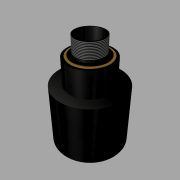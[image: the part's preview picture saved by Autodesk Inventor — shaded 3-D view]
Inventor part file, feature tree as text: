
AUTODESK INVENTOR PART (.ipt)
format: ipt  version: 2019 (Build 230136000, 136)  size: 198,144 bytes
history: native  units: mm
features: sketch x11, extrude x8, other x3, revolve x2, thread x1
ambient origin geometry x8: Origin, YZ Plane, XZ Plane, XY Plane, X Axis, Y Axis, Z Axis, Center Point
bodies: Solid1 (feature_tree), Solid2 (feature_tree), Solid3 (feature_tree), Solid4 (feature_tree)
feature tree (25):
  extrude  "Extrusion1"  Depth=7.0mm
  thread  "Thread1"  [1 undecoded]
  extrude  "Extrusion2"  Depth=15.0mm
  extrude  "Extrusion3"  Depth=0.25mm
  extrude  "Extrusion4"  Depth=0.25mm TaperAngle=0.0deg
  extrude  "Extrusion5"  Depth=19.0mm
  extrude  "Extrusion6"  Depth=10.5mm
  extrude  "Extrusion7"  Depth=4.0mm TaperAngle=0.0deg
  other  "Large Optic"
  extrude  "Extrusion8"  Depth=20.0mm TaperAngle=0.0deg
  other  "Large Optic Lens"
  sketch  "Sketch9"  dims[d25=-5.0mm d26=0.15mm]
  revolve  "Revolution1"  [1 undecoded]
  other  "Small Optic Lens"
  revolve  "Revolution2"  [1 undecoded]
  sketch  "Sketch1"  dims[d0=11.85mm d1=0.6mm d2=7.0mm d3=0.0mm]
  sketch  "Sketch2"  dims[d4=6.0mm d5=1.0mm d6=15.0mm]
  sketch  "Sketch3"  dims[d7=0.25mm d8=0.0mm d9=16.75mm]
  sketch  "Sketch4"  dims[d10=13.0mm d11=0.25mm d12=0.0mm]
  sketch  "Sketch5"  dims[d13=0.25mm d14=0.0mm d15=19.0mm]
  sketch  "Sketch6"  dims[d16=10.5mm d17=0.0mm d18=28.5mm]
  sketch  "Sketch7"  dims[d19=1.0mm d20=4.0mm d21=0.0mm]
  sketch  "Sketch8"  dims[d22=1.5mm d23=20.0mm d24=0.0mm]
  sketch  "Sketch10"  dims[d27=1.5mm d28=4.0mm d29=0.0mm]
  sketch  "Sketch12"  dims[d30=1.333mm d31=90.0deg d32=-0.5mm d33=1.0mm d34=90.0deg]
note: 3 required parameter values undecoded (feature->parameter linkage not recoverable at this tier; creation-order binding heuristic only, values carry confidence <= 0.55)